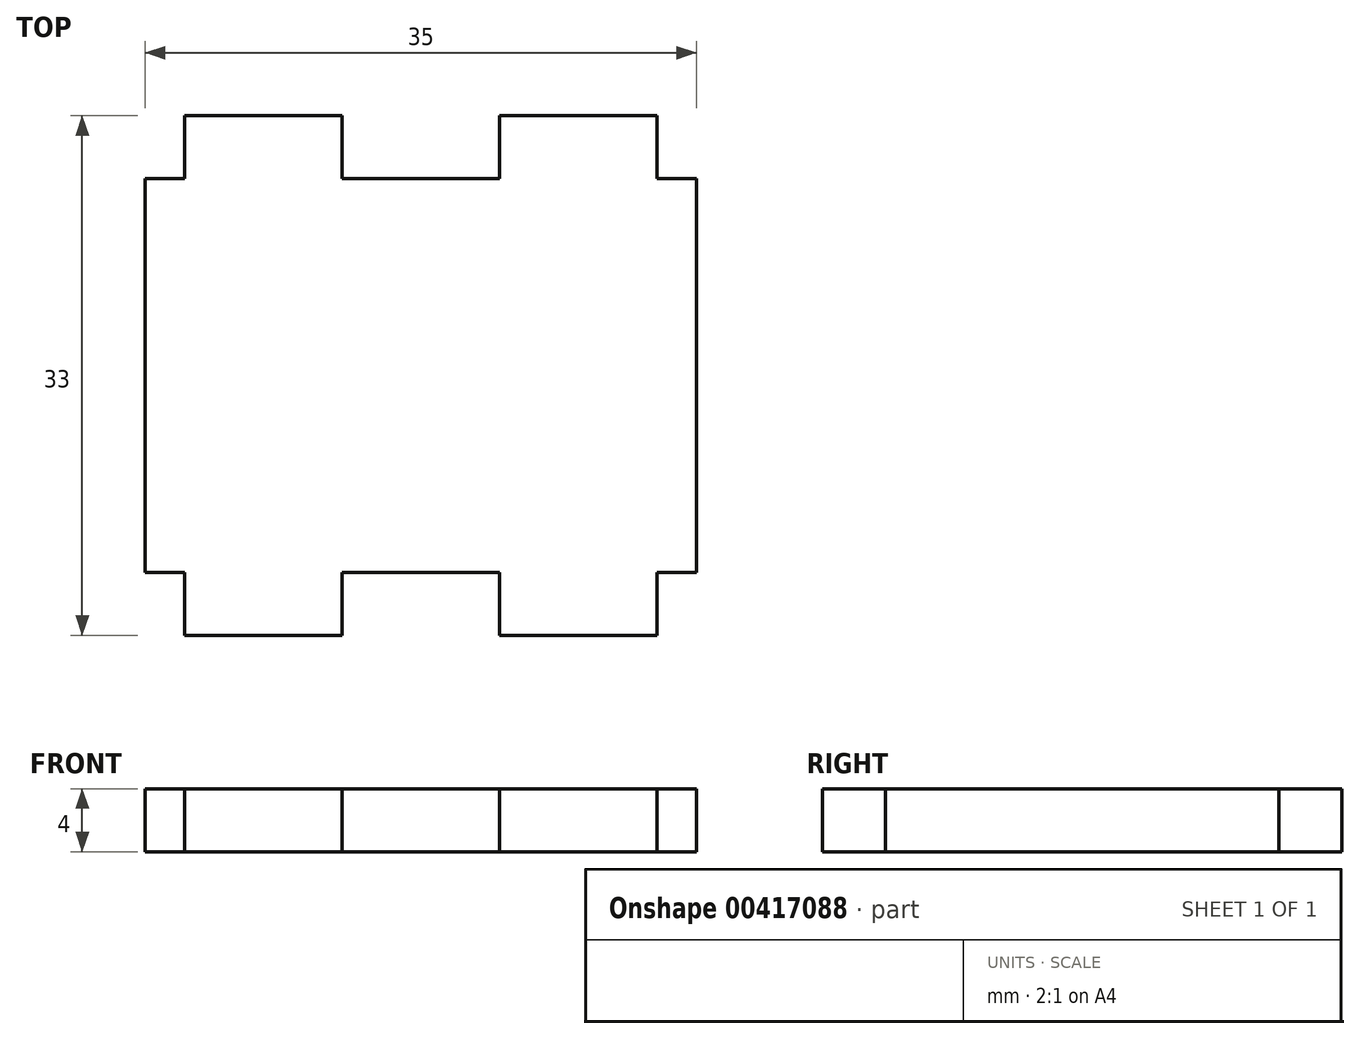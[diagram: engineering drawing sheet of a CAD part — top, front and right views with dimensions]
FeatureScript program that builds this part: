
annotation { "Feature Type Name" : "Feature", "Feature Type Description" : "" }
export const myFeature = defineFeature(function(context is Context, id is Id, definition is map)
    precondition{}
    {
        {
            var Q0;
            Q0=qCreatedBy(makeId("Top.planeOp"),FACE);
            var sketch = newSketch(context, id + "F0", { "sketchPlane" : qUnion([Q0])});
            skLineSegment(sketch, "E0", {"start": v(-17.5, 0) * mm, "end": v(-17.5, -12.5) * mm});
            skLineSegment(sketch, "E1", {"start": v(-17.5, -12.5) * mm, "end": v(-15, -12.5) * mm});
            skLineSegment(sketch, "E2", {"start": v(-15, -12.5) * mm, "end": v(-15, -16.5) * mm});
            skLineSegment(sketch, "E3", {"start": v(-15, -16.5) * mm, "end": v(-5, -16.5) * mm});
            skLineSegment(sketch, "E4", {"start": v(-5, -16.5) * mm, "end": v(-5, -12.5) * mm});
            skLineSegment(sketch, "E5", {"start": v(-5, -12.5) * mm, "end": v(0, -12.5) * mm});
            skLineSegment(sketch, "E6.MirrorCS", {"start": v(5, -12.5) * mm, "end": v(0, -12.5) * mm});
            skLineSegment(sketch, "E7.MirrorCS", {"start": v(17.5, 0) * mm, "end": v(17.5, -12.5) * mm});
            skLineSegment(sketch, "E8.MirrorCS", {"start": v(5, -16.5) * mm, "end": v(5, -12.5) * mm});
            skLineSegment(sketch, "E9.MirrorCS", {"start": v(15, -12.5) * mm, "end": v(15, -16.5) * mm});
            skLineSegment(sketch, "E10.MirrorCS", {"start": v(15, -16.5) * mm, "end": v(5, -16.5) * mm});
            skLineSegment(sketch, "E11.MirrorCS", {"start": v(17.5, -12.5) * mm, "end": v(15, -12.5) * mm});
            skLineSegment(sketch, "E12.MirrorCS", {"start": v(17.5, 12.5) * mm, "end": v(15, 12.5) * mm});
            skLineSegment(sketch, "E13.MirrorCS", {"start": v(15, 12.5) * mm, "end": v(15, 16.5) * mm});
            skLineSegment(sketch, "E14.MirrorCS", {"start": v(5, 16.5) * mm, "end": v(5, 12.5) * mm});
            skLineSegment(sketch, "E15.MirrorCS", {"start": v(5, 12.5) * mm, "end": v(0, 12.5) * mm});
            skLineSegment(sketch, "E16.MirrorCS", {"start": v(-15, 12.5) * mm, "end": v(-15, 16.5) * mm});
            skLineSegment(sketch, "E17.MirrorCS", {"start": v(-17.5, 12.5) * mm, "end": v(-15, 12.5) * mm});
            skLineSegment(sketch, "E18.MirrorCS", {"start": v(-5, 16.5) * mm, "end": v(-5, 12.5) * mm});
            skLineSegment(sketch, "E19.MirrorCS", {"start": v(-5, 12.5) * mm, "end": v(0, 12.5) * mm});
            skLineSegment(sketch, "E20.MirrorCS", {"start": v(15, 16.5) * mm, "end": v(5, 16.5) * mm});
            skLineSegment(sketch, "E21.MirrorCS", {"start": v(17.5, 0) * mm, "end": v(17.5, 12.5) * mm});
            skLineSegment(sketch, "E22.MirrorCS", {"start": v(-17.5, 0) * mm, "end": v(-17.5, 12.5) * mm});
            skLineSegment(sketch, "E23.MirrorCS", {"start": v(-15, 16.5) * mm, "end": v(-5, 16.5) * mm});
            skSolve(sketch);
        }
        {
            var Q0;
            Q0=makeQuery(id+"F0.imprint","IMPRINT",FACE,{"disambiguationData":[TD([[makeQuery(id+"F0.imprint","IMPRINT",EDGE,{"derivedFrom":sQuery(id+"F0.wireOp",EDGE,"E0")}),1.0]])]});
            extrude(context, id + "F1", {"entities" : qUnion([Q0]), "depth" : 4 * mm});
        }
    });
